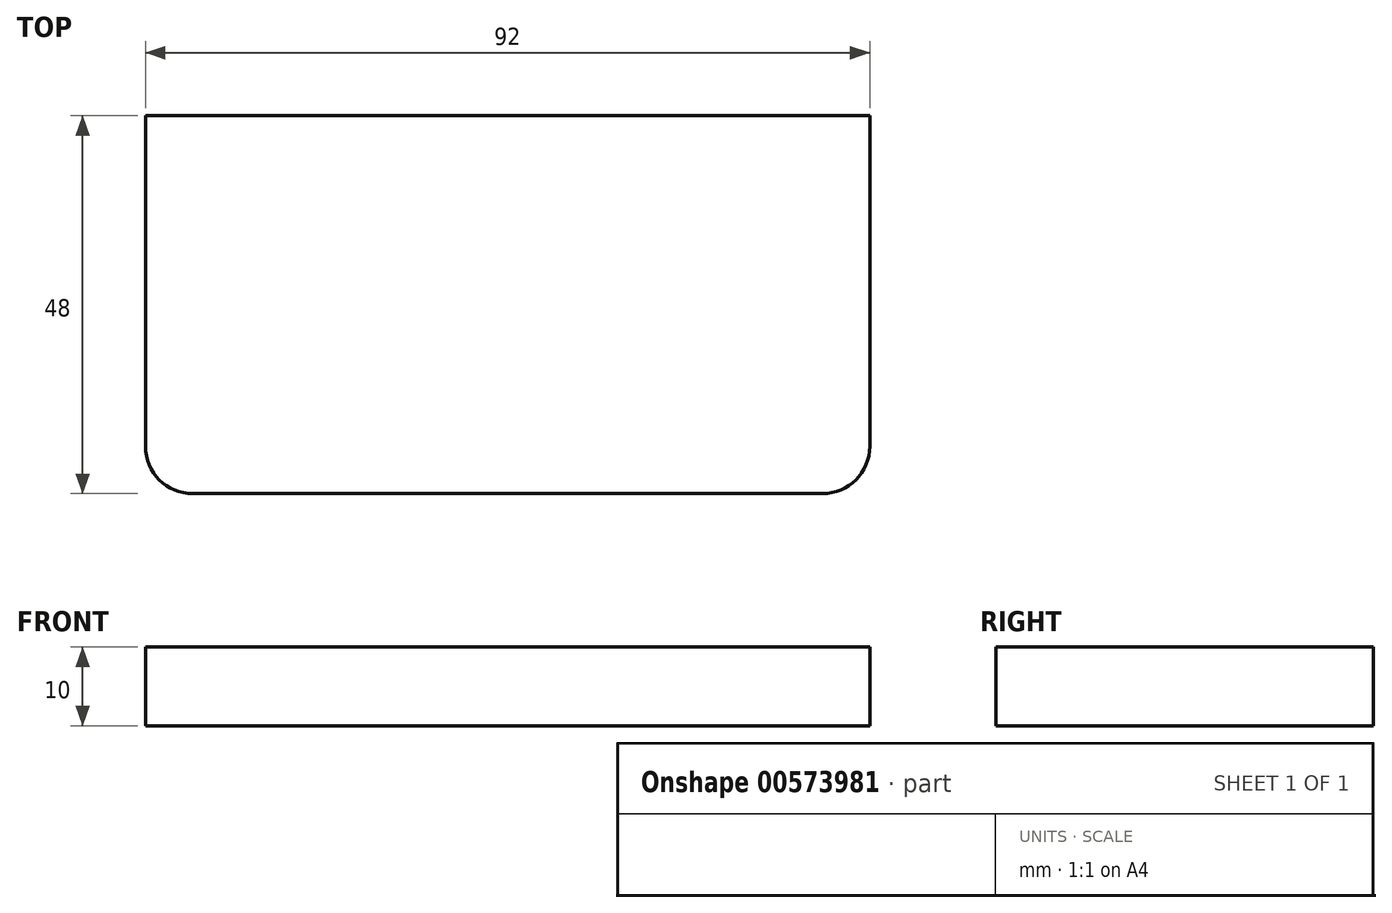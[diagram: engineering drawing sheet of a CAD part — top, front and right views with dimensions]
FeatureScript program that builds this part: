
annotation { "Feature Type Name" : "Feature", "Feature Type Description" : "" }
export const myFeature = defineFeature(function(context is Context, id is Id, definition is map)
    precondition{}
    {
        {
            var Q0;
            Q0=qCreatedBy(makeId("Top.planeOp"),FACE);
            var sketch = newSketch(context, id + "F0", { "sketchPlane" : qUnion([Q0])});
            skLineSegment(sketch, "E0.bottom", {"start": v(-46, 30) * mm, "end": v(46, 30) * mm});
            skLineSegment(sketch, "E0.top", {"start": v(-40, -18) * mm, "end": v(40, -18) * mm});
            skLineSegment(sketch, "E0.left", {"start": v(-46, 30) * mm, "end": v(-46, -12) * mm});
            skLineSegment(sketch, "E0.right", {"start": v(46, 30) * mm, "end": v(46, -12) * mm});
            skPoint(sketch, "E1.visualSharp", {"position": v(-46, -18) * mm});
            skArc(sketch, "E1.filletArc", {"start": v(-46, -12) * mm, "mid": v(-44.24, -16.24) * mm, "end": v(-40, -18) * mm});
            skPoint(sketch, "E2.visualSharp", {"position": v(46, -18) * mm});
            skArc(sketch, "E2.filletArc", {"start": v(40, -18) * mm, "mid": v(44.24, -16.24) * mm, "end": v(46, -12) * mm});
            skSolve(sketch);
        }
        {
            var Q0;
            Q0=makeQuery(id+"F0.imprint","IMPRINT",FACE,{"disambiguationData":[TD([[makeQuery(id+"F0.imprint","IMPRINT",EDGE,{"derivedFrom":sQuery(id+"F0.wireOp",EDGE,"E0.bottom")}),-1.0]])]});
            extrude(context, id + "F1", {"entities" : qUnion([Q0]), "depth" : 10 * mm, "offsetDistance" : 25 * mm});
        }
    });
